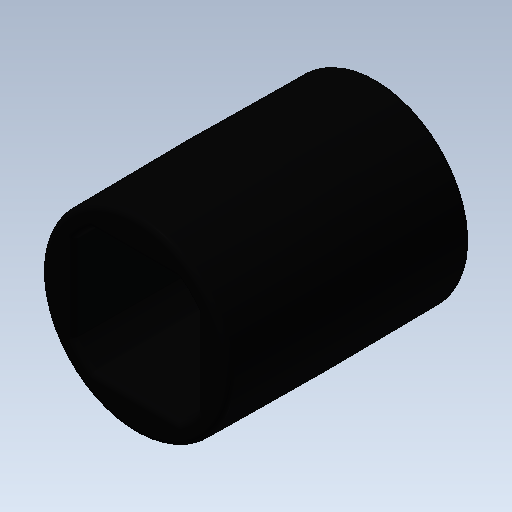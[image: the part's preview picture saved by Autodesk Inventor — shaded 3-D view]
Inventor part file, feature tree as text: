
AUTODESK INVENTOR PART (.ipt)
format: ipt  version: 2020 (Build 240168000, 168)  size: 261,632 bytes
history: native  units: in
note: dims shown in document units (in); Inventor stores cm internally (conversion verified against a paired STEP export)
features: other x1, fillet x1, imported_body x1
ambient origin geometry x8: Origin, YZ Plane, XZ Plane, XY Plane, X Axis, Y Axis, Z Axis, Center Point
bodies: Body1 (feature_tree)
feature tree (3):
  other  "Spacer HS 1.0 unit"
  fillet  "Fillet1"  [1 undecoded]
  imported_body  "Base1"
note: 1 required parameter value undecoded (feature->parameter linkage not recoverable at this tier; creation-order binding heuristic only, values carry confidence <= 0.55)
